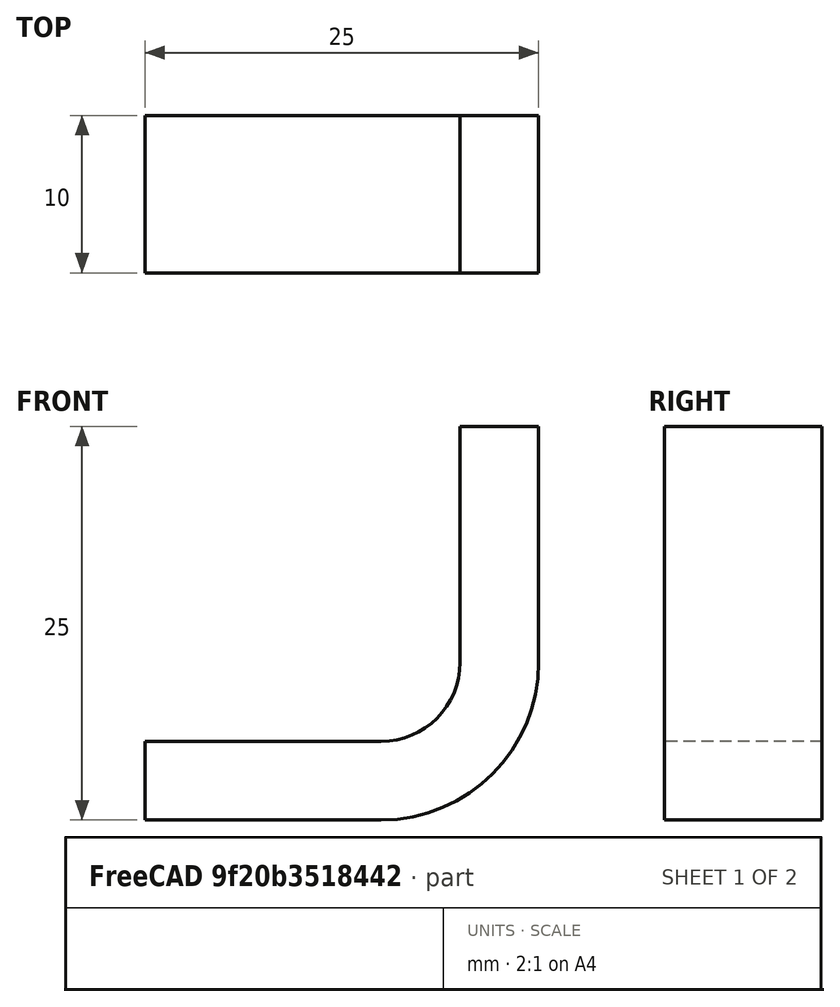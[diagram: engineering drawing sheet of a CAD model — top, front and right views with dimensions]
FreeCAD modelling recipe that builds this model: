
FCSTD DOCUMENT  (FreeCAD 2023.131R26244 +5365 (Git))
Label: simple
License: Creative Commons Attribution
LicenseURL: http://creativecommons.org/licenses/by/4.0/
objects: Sketcher::SketchObject×1, PartDesign::Pad×1, PartDesign::Body×1
note: 6 computed .brp shape members not serialized (recipe doc carries the construction recipe); baked Part::Feature solids carry a one-line shape summary decoded from their .brp

FEATURE [Sketcher::SketchObject] Sketch
  ArcFitTolerance = 1e-06
  AttachmentSupport = -> [XZ_Plane]
  ExternalBSplineMaxDegree = 5
  ExternalBSplineTolerance = 0.0001
  FixShape = 1
  FullyConstrained = true
  InternalTolerance = 1e-06
  InvalidShape = false
  MakeInternals = false
  MapMode = 5
  Placement = pos=(0,0,0) rot=(1,0,0;1.5708rad)
  Support = -> [XZ_Plane]
  TreeRank = 11
  ValidateShape = false
  sketch-geometry (8):
    g0: LineSegment StartX=0 StartY=0 StartZ=0 EndX=15 EndY=0 EndZ=0
    g1: ArcOfCircle CenterX=15 CenterY=5 CenterZ=0 NormalX=0 NormalY=0 NormalZ=1 AngleXU=0 Radius=5 StartAngle=4.71239 EndAngle=6.28319
    g2: LineSegment StartX=20 StartY=5 StartZ=0 EndX=20 EndY=20 EndZ=0
    g3: LineSegment StartX=20 StartY=20 StartZ=0 EndX=25 EndY=20 EndZ=0
    g4: LineSegment StartX=25 StartY=20 StartZ=0 EndX=25 EndY=5 EndZ=0
    g5: ArcOfCircle CenterX=15 CenterY=5 CenterZ=0 NormalX=0 NormalY=0 NormalZ=1 AngleXU=0 Radius=10 StartAngle=4.71239 EndAngle=6.28319
    g6: LineSegment StartX=15 StartY=-5 StartZ=0 EndX=0 EndY=-5 EndZ=0
    g7: LineSegment StartX=0 StartY=-5 StartZ=0 EndX=0 EndY=0 EndZ=0
  constraints (20):
    c: Coincident(g-1,g0)
    c: PointOnObject(g0,g-1)
    c: Tangent(g0,g1) = -1.5708
    c: Tangent(g1,g2) = -1.5708
    c: Coincident(g2,g3)
    c: Horizontal(g3)
    c: Coincident(g3,g4)
    c: Vertical(g4)
    c: Tangent(g4,g5) = 1.5708
    c: Tangent(g5,g6) = 1.5708
    c: Coincident(g6,g7)
    c: Coincident(g7,g0)
    c: Coincident(g5,g1)
    c: Vertical(g7)
    c: Vertical(g2)
    c: Horizontal(g6)
    c: DistanceX(g3,g3) = 5
    c: Equal(g2,g0)
    c: DistanceX(g0,g0) = 15
    c: Radius(g1) = 5
FEATURE [PartDesign::Pad] Pad
  AddSubType = 0
  AlongSketchNormal = false
  AutoTaperInnerAngle = true
  CheckUpToFaceLimits = true
  ClaimChildren = false
  Direction = (0,-1,2e-16)
  Fit = 0
  FitJoin = 0
  FixShape = 1
  InnerFit = 0
  InnerFitJoin = 0
  InvalidShape = false
  Length = 10
  Length2 = 100
  Linearize = true
  NewSolid = false
  Profile = -> Sketch
  Suppress = false
  TaperInnerAngle = 0
  TaperInnerAngleRev = 0
  TreeRank = 12
  Type = 0
  ValidateShape = false
  _ProfileBasedVersion = 1
FEATURE [PartDesign::Body] Body
  AutoGroupSolids = false
  ClaimAllChildren = false
  ExportMode = 0
  FixShape = 1
  Group = -> [Sketch,Pad]
  InvalidShape = false
  Origin = -> Origin
  Tip = -> Pad
  TreeRank = 10
  ValidateShape = false
  _ExportChildren = -> [Pad]
  _GroupVersion = 1
